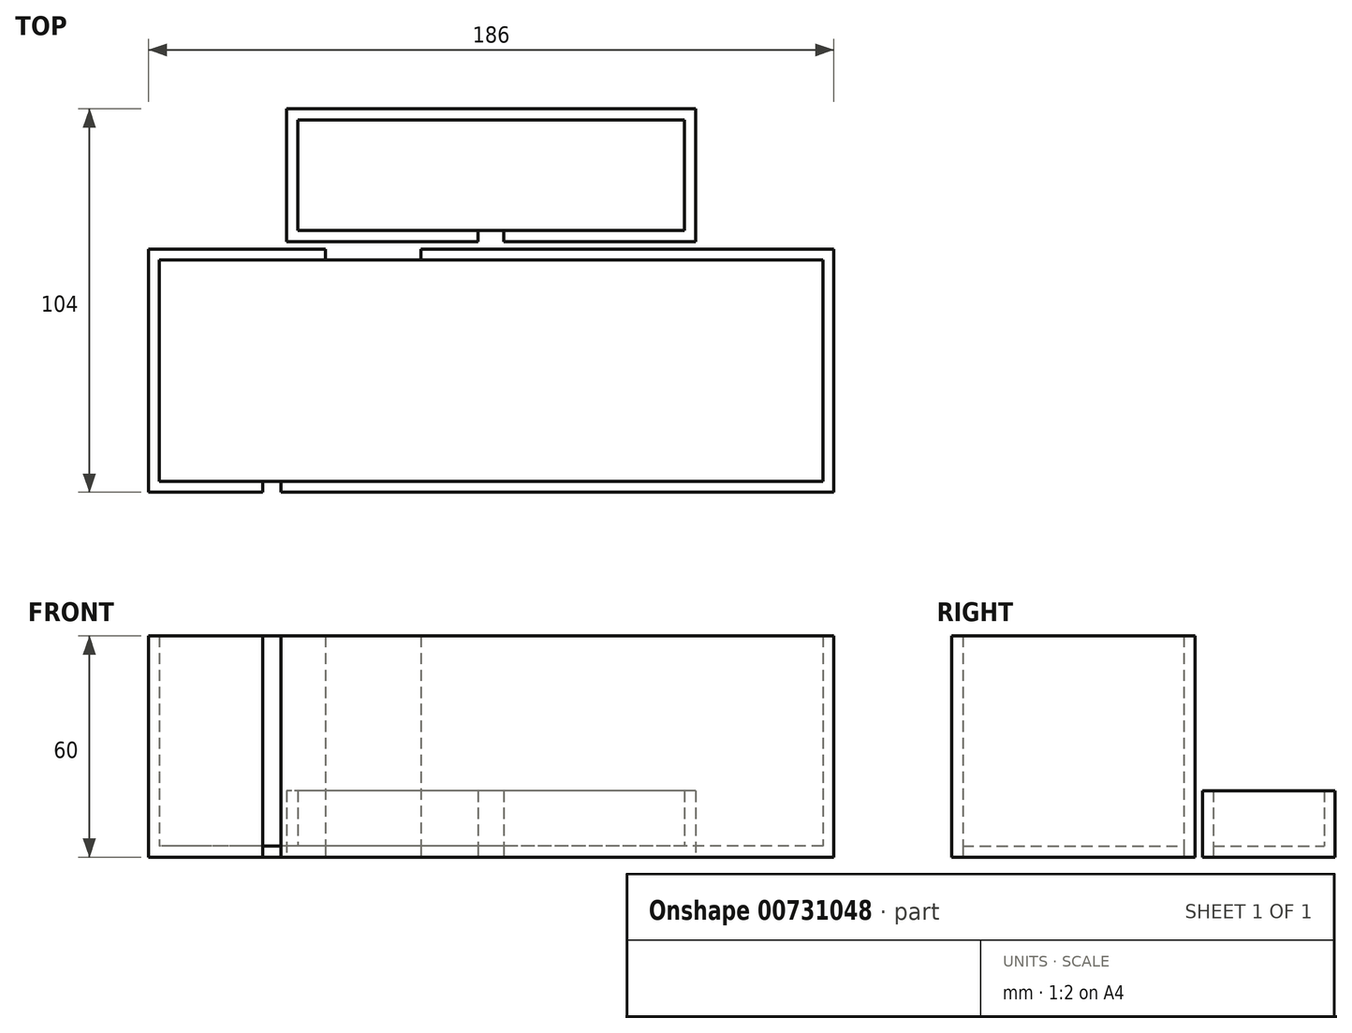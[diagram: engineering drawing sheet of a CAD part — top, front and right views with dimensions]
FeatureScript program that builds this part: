
annotation { "Feature Type Name" : "Feature", "Feature Type Description" : "" }
export const myFeature = defineFeature(function(context is Context, id is Id, definition is map)
    precondition{}
    {
        {
            var Q0;
            Q0=qCreatedBy(makeId("Top.planeOp"),FACE);
            var sketch = newSketch(context, id + "F0", { "sketchPlane" : qUnion([Q0])});
            skLineSegment(sketch, "E0.bottom", {"start": v(90, -30) * mm, "end": v(-90, -30) * mm});
            skLineSegment(sketch, "E0.top", {"start": v(90, 30) * mm, "end": v(-90, 30) * mm});
            skLineSegment(sketch, "E0.left", {"start": v(90, -30) * mm, "end": v(90, 30) * mm});
            skLineSegment(sketch, "E0.right", {"start": v(-90, -30) * mm, "end": v(-90, 30) * mm});
            skPoint(sketch, "E0.middle", {"position": v(0, 0) * mm});
            skLineSegment(sketch, "E1.0", {"start": v(93, 33) * mm, "end": v(-93, 33) * mm});
            skLineSegment(sketch, "E1.1", {"start": v(93, -33) * mm, "end": v(93, 33) * mm});
            skLineSegment(sketch, "E1.2", {"start": v(93, -33) * mm, "end": v(-93, -33) * mm});
            skLineSegment(sketch, "E1.3", {"start": v(-93, -33) * mm, "end": v(-93, 33) * mm});
            skLineSegment(sketch, "E2.bottom", {"start": v(-62, -30) * mm, "end": v(-57, -30) * mm});
            skLineSegment(sketch, "E2.top", {"start": v(-62, -33) * mm, "end": v(-57, -33) * mm});
            skLineSegment(sketch, "E2.left", {"start": v(-62, -30) * mm, "end": v(-62, -33) * mm});
            skLineSegment(sketch, "E2.right", {"start": v(-57, -30) * mm, "end": v(-57, -33) * mm});
            skLineSegment(sketch, "E3.bottom", {"start": v(-45, 33) * mm, "end": v(-19, 33) * mm});
            skLineSegment(sketch, "E3.top", {"start": v(-45, 30) * mm, "end": v(-19, 30) * mm});
            skLineSegment(sketch, "E3.left", {"start": v(-45, 33) * mm, "end": v(-45, 30) * mm});
            skLineSegment(sketch, "E3.right", {"start": v(-19, 33) * mm, "end": v(-19, 30) * mm});
            skSolve(sketch);
        }
        {
            var Q0;
            Q0=qCreatedBy(makeId("Top.planeOp"),FACE);
            var sketch = newSketch(context, id + "F1", { "sketchPlane" : qUnion([Q0])});
            skLineSegment(sketch, "E4.bottom", {"start": v(52.5, 38) * mm, "end": v(-52.5, 38) * mm});
            skLineSegment(sketch, "E4.top", {"start": v(52.5, 68) * mm, "end": v(-52.5, 68) * mm});
            skLineSegment(sketch, "E4.left", {"start": v(52.5, 38) * mm, "end": v(52.5, 68) * mm});
            skLineSegment(sketch, "E4.right", {"start": v(-52.5, 38) * mm, "end": v(-52.5, 68) * mm});
            skPoint(sketch, "E4.middle", {"position": v(0, 53) * mm});
            skLineSegment(sketch, "E5.0", {"start": v(55.5, 71) * mm, "end": v(-55.5, 71) * mm});
            skLineSegment(sketch, "E5.1", {"start": v(55.5, 35) * mm, "end": v(55.5, 71) * mm});
            skLineSegment(sketch, "E5.2", {"start": v(55.5, 35) * mm, "end": v(-55.5, 35) * mm});
            skLineSegment(sketch, "E5.3", {"start": v(-55.5, 35) * mm, "end": v(-55.5, 71) * mm});
            skLineSegment(sketch, "E6.bottom", {"start": v(3.5, 35) * mm, "end": v(-3.5, 35) * mm});
            skLineSegment(sketch, "E6.top", {"start": v(3.5, 38) * mm, "end": v(-3.5, 38) * mm});
            skLineSegment(sketch, "E6.left", {"start": v(3.5, 35) * mm, "end": v(3.5, 38) * mm});
            skLineSegment(sketch, "E6.right", {"start": v(-3.5, 35) * mm, "end": v(-3.5, 38) * mm});
            skPoint(sketch, "E6.middle", {"position": v(0, 36.5) * mm});
            skPoint(sketch, "E6.middle.positionSnap0", {"position": v(0, 35) * mm});
            skPoint(sketch, "E6.centerSnap0", {"position": v(0, 35) * mm});
            skSolve(sketch);
        }
        {
            var Q0;
            Q0=makeQuery(id+"F1.imprint","IMPRINT",FACE,{"disambiguationData":[TD([[makeQuery(id+"F1.imprint","IMPRINT",EDGE,{"derivedFrom":sQuery(id+"F1.wireOp",EDGE,"E4.top")}),1.0]])]});
            extrude(context, id + "F2", {"entities" : qUnion([Q0]), "depth" : 3 * mm, "offsetDistance" : 25 * mm});
        }
        {
            var Q0;
            Q0=qCreatedBy(makeId("Top.planeOp"),FACE);
            var sketch = newSketch(context, id + "F3", { "sketchPlane" : qUnion([Q0])});
            skLineSegment(sketch, "E7.bottom", {"start": v(52.5, 38) * mm, "end": v(-52.5, 38) * mm});
            skLineSegment(sketch, "E7.top", {"start": v(52.5, 68) * mm, "end": v(-52.5, 68) * mm});
            skLineSegment(sketch, "E7.left", {"start": v(52.5, 38) * mm, "end": v(52.5, 68) * mm});
            skLineSegment(sketch, "E7.right", {"start": v(-52.5, 38) * mm, "end": v(-52.5, 68) * mm});
            skPoint(sketch, "E7.middle", {"position": v(0, 53) * mm});
            skLineSegment(sketch, "E8.0", {"start": v(55.5, 71) * mm, "end": v(-55.5, 71) * mm});
            skLineSegment(sketch, "E8.1", {"start": v(55.5, 35) * mm, "end": v(55.5, 71) * mm});
            skLineSegment(sketch, "E8.2", {"start": v(55.5, 35) * mm, "end": v(-55.5, 35) * mm});
            skLineSegment(sketch, "E8.3", {"start": v(-55.5, 35) * mm, "end": v(-55.5, 71) * mm});
            skLineSegment(sketch, "E9.bottom", {"start": v(3.5, 35) * mm, "end": v(-3.5, 35) * mm});
            skLineSegment(sketch, "E9.top", {"start": v(3.5, 38) * mm, "end": v(-3.5, 38) * mm});
            skLineSegment(sketch, "E9.left", {"start": v(3.5, 35) * mm, "end": v(3.5, 38) * mm});
            skLineSegment(sketch, "E9.right", {"start": v(-3.5, 35) * mm, "end": v(-3.5, 38) * mm});
            skPoint(sketch, "E9.middle", {"position": v(0, 36.5) * mm});
            skPoint(sketch, "E9.middle.positionSnap0", {"position": v(0, 35) * mm});
            skPoint(sketch, "E9.centerSnap0", {"position": v(0, 35) * mm});
            skSolve(sketch);
        }
        {
            var Q0;
            Q0=makeQuery(id+"F3.imprint","IMPRINT",FACE,{"disambiguationData":[TD([[makeQuery(id+"F3.imprint","IMPRINT",EDGE,{"derivedFrom":sQuery(id+"F3.wireOp",EDGE,"E7.top")}),-1.0]])]});
            extrude(context, id + "F4", {"entities" : qUnion([Q0]), "operationType" : NewBodyOperationType.ADD, "depth" : 18 * mm, "offsetDistance" : 25 * mm});
        }
        {
            var Q0;
            {var subQ3=sQuery(id+"F0.wireOp",EDGE,"E0.left");Q0=makeQuery(id+"F0.imprint","IMPRINT",FACE,{"disambiguationData":[TD([[makeQuery(id+"F0.imprint","IMPRINT",EDGE,{"derivedFrom":subQ3}),1.0]])]});}
            var Q1;
            Q1=makeQuery(id+"F0.imprint","IMPRINT",FACE,{"disambiguationData":[TD([[makeQuery(id+"F0.imprint","IMPRINT",EDGE,{"derivedFrom":sQuery(id+"F0.wireOp",EDGE,"E2.bottom")}),-1.0]])]});
            var Q2;
            Q2=makeQuery(id+"F0.imprint","IMPRINT",FACE,{"disambiguationData":[TD([[makeQuery(id+"F0.imprint","IMPRINT",EDGE,{"derivedFrom":sQuery(id+"F0.wireOp",EDGE,"E3.bottom")}),-1.0]])]});
            extrude(context, id + "F5", {"entities" : qUnion([Q0, Q1, Q2]), "depth" : 3 * mm, "offsetDistance" : 25 * mm});
        }
        {
            var Q0;
            Q0=qCreatedBy(makeId("Top.planeOp"),FACE);
            var sketch = newSketch(context, id + "F6", { "sketchPlane" : qUnion([Q0])});
            skLineSegment(sketch, "E10.bottom", {"start": v(90, -30) * mm, "end": v(-90, -30) * mm});
            skLineSegment(sketch, "E10.top", {"start": v(90, 30) * mm, "end": v(-90, 30) * mm});
            skLineSegment(sketch, "E10.left", {"start": v(90, -30) * mm, "end": v(90, 30) * mm});
            skLineSegment(sketch, "E10.right", {"start": v(-90, -30) * mm, "end": v(-90, 30) * mm});
            skPoint(sketch, "E10.middle", {"position": v(0, 0) * mm});
            skLineSegment(sketch, "E11.0", {"start": v(93, 33) * mm, "end": v(-93, 33) * mm});
            skLineSegment(sketch, "E11.1", {"start": v(93, -33) * mm, "end": v(93, 33) * mm});
            skLineSegment(sketch, "E11.2", {"start": v(93, -33) * mm, "end": v(-93, -33) * mm});
            skLineSegment(sketch, "E11.3", {"start": v(-93, -33) * mm, "end": v(-93, 33) * mm});
            skLineSegment(sketch, "E12.bottom", {"start": v(-62, -30) * mm, "end": v(-57, -30) * mm});
            skLineSegment(sketch, "E12.top", {"start": v(-62, -33) * mm, "end": v(-57, -33) * mm});
            skLineSegment(sketch, "E12.left", {"start": v(-62, -30) * mm, "end": v(-62, -33) * mm});
            skLineSegment(sketch, "E12.right", {"start": v(-57, -30) * mm, "end": v(-57, -33) * mm});
            skLineSegment(sketch, "E13.bottom", {"start": v(-45, 33) * mm, "end": v(-19, 33) * mm});
            skLineSegment(sketch, "E13.top", {"start": v(-45, 30) * mm, "end": v(-19, 30) * mm});
            skLineSegment(sketch, "E13.left", {"start": v(-45, 33) * mm, "end": v(-45, 30) * mm});
            skLineSegment(sketch, "E13.right", {"start": v(-19, 33) * mm, "end": v(-19, 30) * mm});
            skSolve(sketch);
        }
        {
            var Q0;
            {var subQ3=sQuery(id+"F6.wireOp",EDGE,"E10.left");Q0=makeQuery(id+"F6.imprint","IMPRINT",FACE,{"disambiguationData":[TD([[makeQuery(id+"F6.imprint","IMPRINT",EDGE,{"derivedFrom":subQ3}),-1.0]])]});}
            var Q1;
            {var subQ3=sQuery(id+"F6.wireOp",EDGE,"E10.right");Q1=makeQuery(id+"F6.imprint","IMPRINT",FACE,{"disambiguationData":[TD([[makeQuery(id+"F6.imprint","IMPRINT",EDGE,{"derivedFrom":subQ3}),1.0]])]});}
            extrude(context, id + "F7", {"entities" : qUnion([Q0, Q1]), "operationType" : NewBodyOperationType.ADD, "depth" : 60 * mm, "offsetDistance" : 25 * mm});
        }
    });
